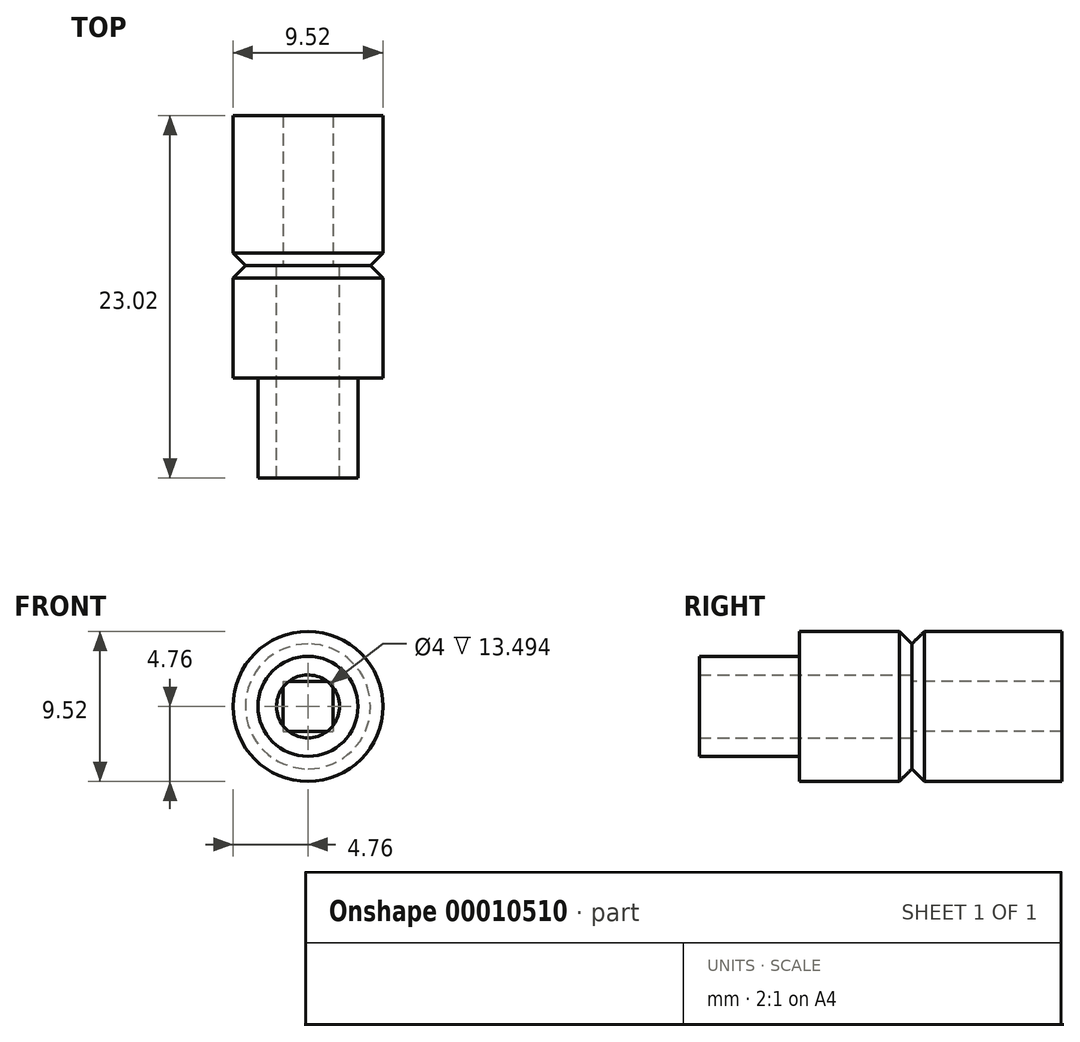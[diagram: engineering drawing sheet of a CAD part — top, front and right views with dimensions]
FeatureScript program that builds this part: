
annotation { "Feature Type Name" : "Feature", "Feature Type Description" : "" }
export const myFeature = defineFeature(function(context is Context, id is Id, definition is map)
    precondition{}
    {
        {
            var Q0;
            Q0=qCreatedBy(makeId("Front.planeOp"),FACE);
            var sketch = newSketch(context, id + "F0", { "sketchPlane" : qUnion([Q0])});
            skCircle(sketch, "E0", {"center": v(0, 0) * mm, "radius": 3.18 * mm});
            skSolve(sketch);
        }
        {
            var Q0;
            Q0 = qSketchRegion(id + "F0", true);
            extrude(context, id + "F1", {"entities" : qUnion([Q0]), "depth" : 6.35 * mm});
        }
        {
            var Q0;
            Q0=qCreatedBy(makeId("Front.planeOp"),FACE);
            var sketch = newSketch(context, id + "F2", { "sketchPlane" : qUnion([Q0])});
            skCircle(sketch, "E1", {"center": v(0, 0) * mm, "radius": 4.76 * mm});
            skSolve(sketch);
        }
        {
            var Q0;
            Q0 = qSketchRegion(id + "F2", true);
            extrude(context, id + "F3", {"entities" : qUnion([Q0]), "operationType" : NewBodyOperationType.ADD, "oppositeDirection" : true, "depth" : 7.14 * mm});
        }
        {
            var Q0;
            Q0=makeQuery(id+"F3.opExtrude","CAP_EDGE",EDGE,{"disambiguationData":[OSD([sQuery(id+"F2.wireOp",EDGE,"E1")])],"isStart":false});
            chamfer(context, id + "F4", {"entities" : qUnion([Q0]), "width" : 0.8 * mm, "tangentPropagation" : true});
        }
        {
            var Q0;
            Q0=makeQuery(id+"F3.opExtrude","CAP_FACE",FACE,{"disambiguationData":[OSD([sQuery(id+"F2.wireOp",EDGE,"E1")])],"isStart":false});
            var sketch = newSketch(context, id + "F5", { "sketchPlane" : qUnion([Q0])});
            skCircle(sketch, "E2", {"center": v(0, 0) * mm, "radius": 2 * mm});
            skSolve(sketch);
        }
        {
            var Q0;
            Q0 = qSketchRegion(id + "F5", true);
            extrude(context, id + "F6", {"entities" : qUnion([Q0]), "operationType" : NewBodyOperationType.REMOVE, "endBound" : BoundingType.THROUGH_ALL, "oppositeDirection" : true, "depth" : 25.4 * mm});
        }
        {
            var Q0;
            Q0=makeQuery(id+"F3.opExtrude","CAP_FACE",FACE,{"disambiguationData":[OSD([sQuery(id+"F2.wireOp",EDGE,"E1")])],"isStart":false});
            var sketch = newSketch(context, id + "F7", { "sketchPlane" : qUnion([Q0])});
            skCircle(sketch, "E3", {"center": v(0, 0) * mm, "radius": 4.76 * mm});
            skLineSegment(sketch, "E4.rect.bottom", {"start": v(1.59, 1.59) * mm, "end": v(-1.59, 1.59) * mm});
            skLineSegment(sketch, "E4.rect.top", {"start": v(1.59, -1.59) * mm, "end": v(-1.59, -1.59) * mm});
            skLineSegment(sketch, "E4.rect.left", {"start": v(1.59, 1.59) * mm, "end": v(1.59, -1.59) * mm});
            skLineSegment(sketch, "E4.rect.right", {"start": v(-1.59, 1.59) * mm, "end": v(-1.59, -1.59) * mm});
            skSolve(sketch);
        }
        {
            var Q0;
            Q0 = qSketchRegion(id + "F7", true);
            extrude(context, id + "F8", {"entities" : qUnion([Q0]), "operationType" : NewBodyOperationType.ADD, "depth" : 9.52 * mm});
        }
        {
            var Q0;
            Q0=makeQuery(id+"F8.opExtrude","CAP_EDGE",EDGE,{"disambiguationData":[OSD([sQuery(id+"F7.wireOp",EDGE,"E3")])],"isStart":true});
            chamfer(context, id + "F9", {"entities" : qUnion([Q0]), "width" : 0.8 * mm, "tangentPropagation" : true});
        }
    });
